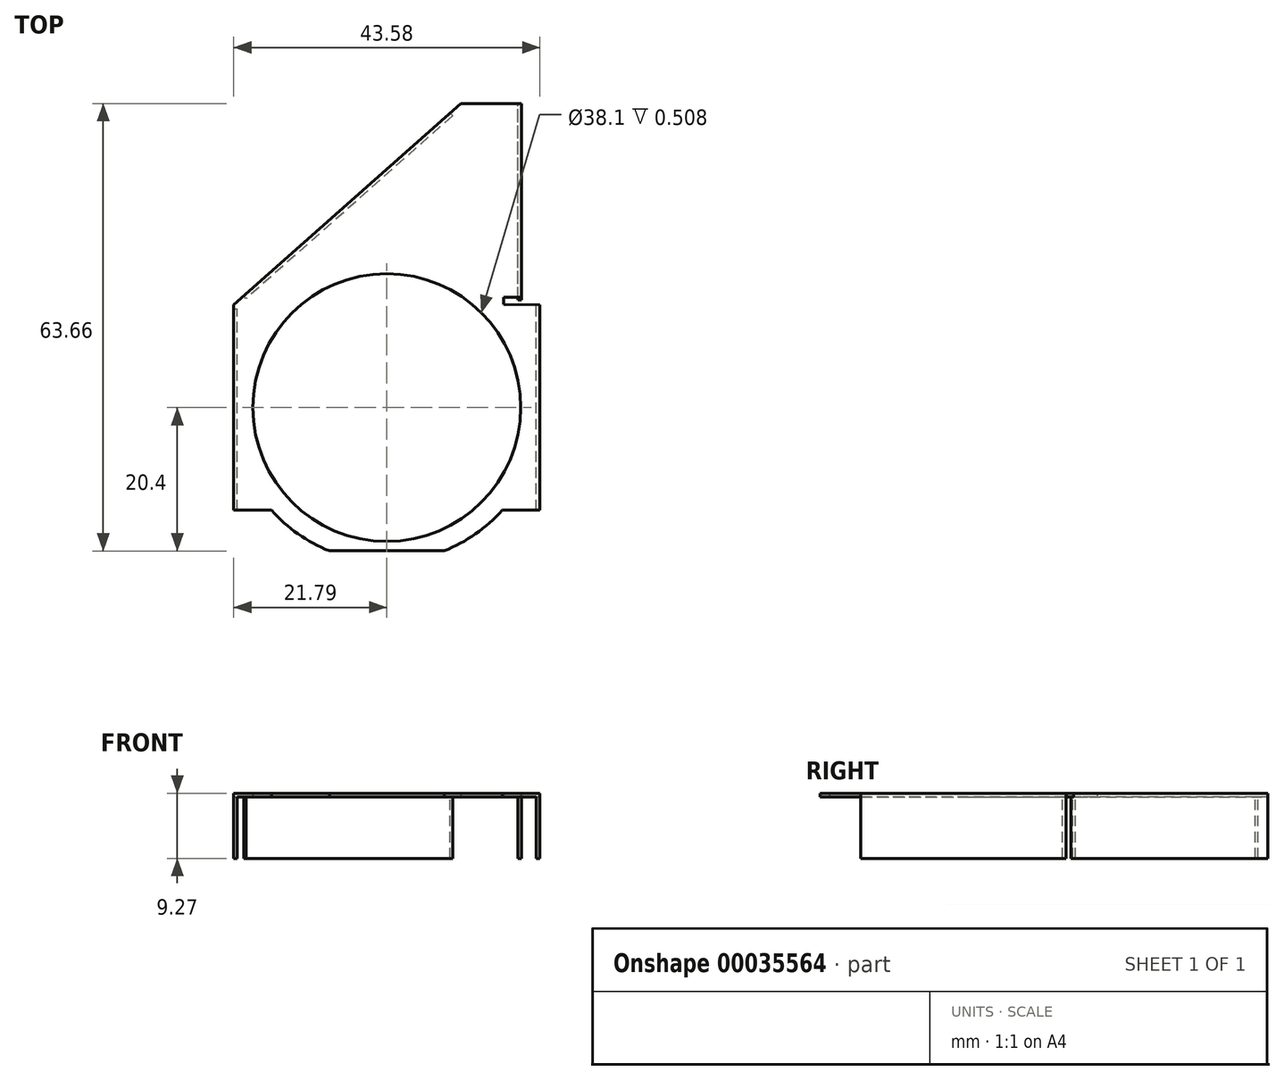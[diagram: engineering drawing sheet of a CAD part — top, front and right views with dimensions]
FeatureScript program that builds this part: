
annotation { "Feature Type Name" : "Feature", "Feature Type Description" : "" }
export const myFeature = defineFeature(function(context is Context, id is Id, definition is map)
    precondition{}
    {
        {
            var Q0;
            Q0=qCreatedBy(makeId("Top.planeOp"),FACE);
            var sketch = newSketch(context, id + "F0", { "sketchPlane" : qUnion([Q0])});
            skCircle(sketch, "E0", {"center": v(0, 0) * mm, "radius": 19.05 * mm});
            skLineSegment(sketch, "E1.rect.top", {"start": v(-21.8, -14.6) * mm, "end": v(-16.41, -14.6) * mm});
            skLineSegment(sketch, "E1.rect.left", {"start": v(-21.8, 14.6) * mm, "end": v(-21.8, -14.6) * mm});
            skLineSegment(sketch, "E1.rect.right", {"start": v(21.8, 14.6) * mm, "end": v(21.8, -14.6) * mm});
            skLineSegment(sketch, "E2", {"start": v(-8.17, -20.4) * mm, "end": v(8.17, -20.4) * mm});
            skLineSegment(sketch, "E3.trimOffspring", {"start": v(16.41, -14.6) * mm, "end": v(21.8, -14.6) * mm});
            skLineSegment(sketch, "E4.trimOffspring", {"start": v(16.6, 14.66) * mm, "end": v(21.8, 14.6) * mm});
            skLineSegment(sketch, "E5", {"start": v(19.18, 43.26) * mm, "end": v(10.54, 43.26) * mm});
            skLineSegment(sketch, "E6", {"start": v(10.54, 43.26) * mm, "end": v(-21.8, 14.6) * mm});
            skLineSegment(sketch, "E7", {"start": v(16.6, 14.66) * mm, "end": v(16.6, 15.68) * mm});
            skLineSegment(sketch, "E8", {"start": v(16.6, 15.68) * mm, "end": v(19.18, 15.68) * mm});
            skLineSegment(sketch, "E9", {"start": v(19.18, 15.68) * mm, "end": v(19.18, 43.26) * mm});
            skArc(sketch, "E10", {"start": v(8.17, -20.4) * mm, "mid": v(12.63, -17.98) * mm, "end": v(16.41, -14.6) * mm});
            skArc(sketch, "E11.trimOffspring", {"start": v(-16.41, -14.6) * mm, "mid": v(-12.63, -17.98) * mm, "end": v(-8.17, -20.4) * mm});
            skSolve(sketch);
        }
        {
            var Q0;
            Q0 = qSketchRegion(id + "F0", true);
            extrude(context, id + "F1", {"entities" : qUnion([Q0]), "depth" : 0.5 * mm});
        }
        {
            var Q0;
            Q0=makeQuery(id+"F1.opExtrude","CAP_FACE",FACE,{"disambiguationData":[OSD([sQuery(id+"F0.wireOp",EDGE,"E0"),sQuery(id+"F0.wireOp",EDGE,"E1.rect.top"),sQuery(id+"F0.wireOp",EDGE,"E1.rect.left"),sQuery(id+"F0.wireOp",EDGE,"E1.rect.right"),sQuery(id+"F0.wireOp",EDGE,"E2"),sQuery(id+"F0.wireOp",EDGE,"67702dcd-46d4-4a7e-8dc7-239cc2453d86"),sQuery(id+"F0.wireOp",EDGE,"f81b3aa4-34ea-4db9-a0a2-ffc185616772"),sQuery(id+"F0.wireOp",EDGE,"E3.trimOffspring"),sQuery(id+"F0.wireOp",EDGE,"E4.trimOffspring"),sQuery(id+"F0.wireOp",EDGE,"b1f17aa3-a624-4172-b463-56570d134e3e"),sQuery(id+"F0.wireOp",EDGE,"E5"),sQuery(id+"F0.wireOp",EDGE,"E6")])],"isStart":true});
            var sketch = newSketch(context, id + "F2", { "sketchPlane" : qUnion([Q0])});
            skLineSegment(sketch, "E12.bottom", {"start": v(-21.8, 14.6) * mm, "end": v(-21.29, 14.6) * mm});
            skLineSegment(sketch, "E12.top", {"start": v(-21.8, -14.07) * mm, "end": v(-21.29, -14.07) * mm});
            skLineSegment(sketch, "E12.left", {"start": v(-21.8, 14.6) * mm, "end": v(-21.8, -14.07) * mm});
            skLineSegment(sketch, "E12.right", {"start": v(-21.29, 14.6) * mm, "end": v(-21.29, -14.07) * mm});
            skLineSegment(sketch, "E13.bottom", {"start": v(21.8, 14.6) * mm, "end": v(21.29, 14.6) * mm});
            skLineSegment(sketch, "E13.top", {"start": v(21.8, -14.6) * mm, "end": v(21.29, -14.6) * mm});
            skLineSegment(sketch, "E13.left", {"start": v(21.8, 14.6) * mm, "end": v(21.8, -14.6) * mm});
            skLineSegment(sketch, "E13.right", {"start": v(21.29, 14.6) * mm, "end": v(21.29, -14.6) * mm});
            skLineSegment(sketch, "E14", {"start": v(9.01, -41.9) * mm, "end": v(9.35, -41.52) * mm});
            skLineSegment(sketch, "E15", {"start": v(9.35, -41.52) * mm, "end": v(-20.01, -15.5) * mm});
            skLineSegment(sketch, "E16", {"start": v(-20.01, -15.5) * mm, "end": v(-20.35, -15.88) * mm});
            skLineSegment(sketch, "E17", {"start": v(-20.35, -15.88) * mm, "end": v(9.01, -41.9) * mm});
            skLineSegment(sketch, "E18", {"start": v(19.18, -15.3) * mm, "end": v(18.67, -15.3) * mm});
            skLineSegment(sketch, "E19", {"start": v(18.67, -15.3) * mm, "end": v(18.67, -43.26) * mm});
            skLineSegment(sketch, "E20", {"start": v(18.67, -43.26) * mm, "end": v(19.18, -43.26) * mm});
            skLineSegment(sketch, "E21", {"start": v(19.18, -43.26) * mm, "end": v(19.18, -15.3) * mm});
            skSolve(sketch);
        }
        {
            var Q0;
            Q0 = qSketchRegion(id + "F2", true);
            extrude(context, id + "F3", {"entities" : qUnion([Q0]), "operationType" : NewBodyOperationType.ADD, "depth" : 8.76 * mm});
        }
    });
